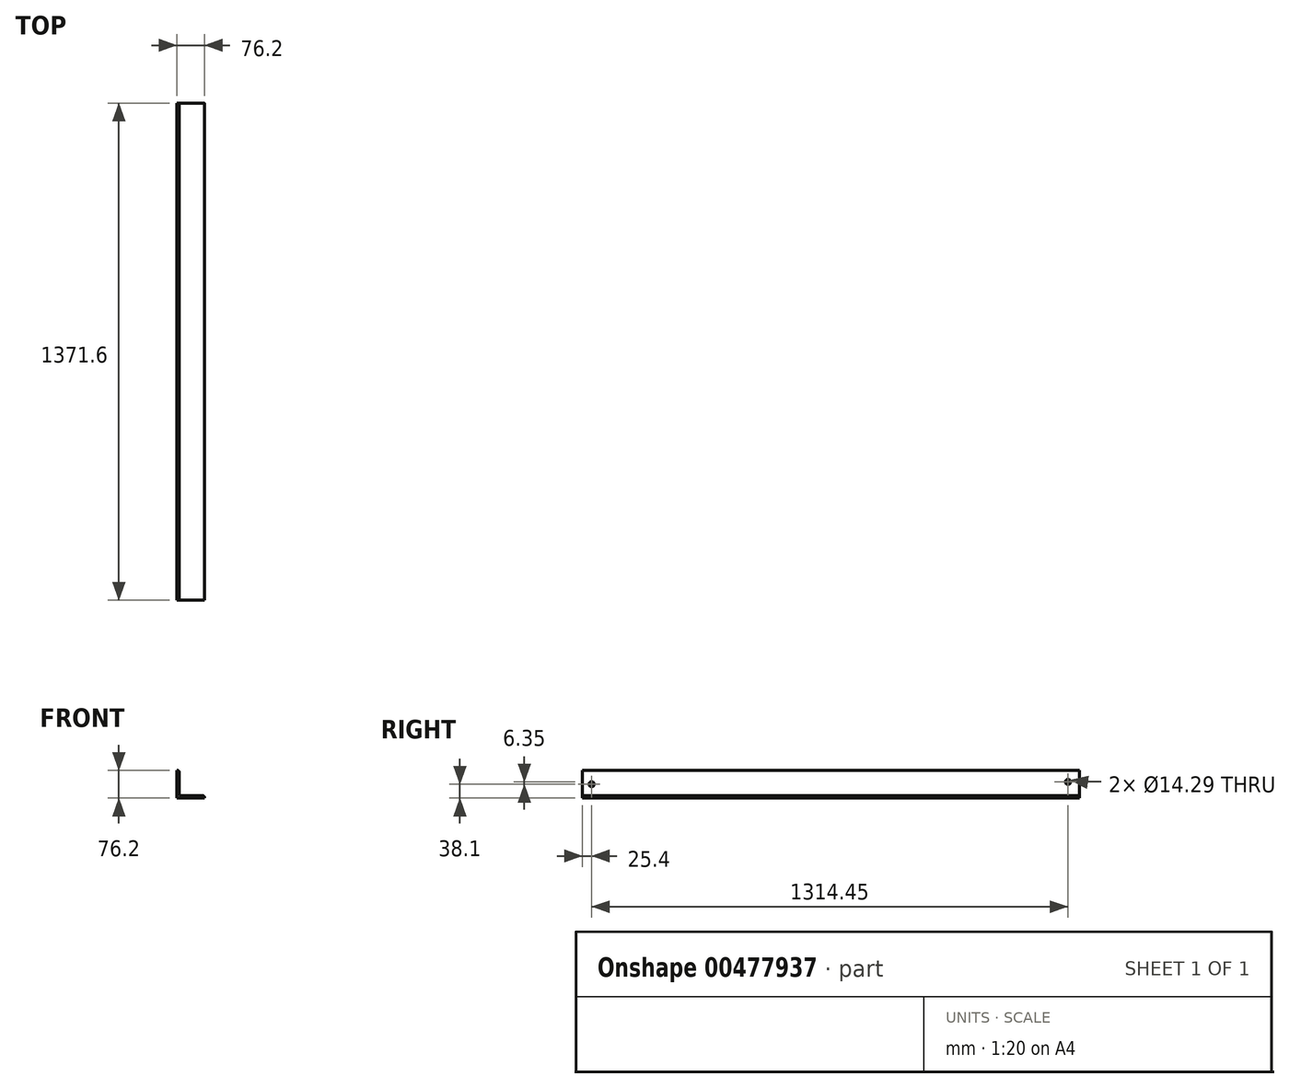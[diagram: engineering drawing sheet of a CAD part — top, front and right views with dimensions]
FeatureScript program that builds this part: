
annotation { "Feature Type Name" : "Feature", "Feature Type Description" : "" }
export const myFeature = defineFeature(function(context is Context, id is Id, definition is map)
    precondition{}
    {
        {
            var Q0;
            Q0=qCreatedBy(makeId("Front.planeOp"),FACE);
            var sketch = newSketch(context, id + "F0", { "sketchPlane" : qUnion([Q0])});
            skLineSegment(sketch, "E0.bottom", {"start": v(-31.75, 38.1) * mm, "end": v(-38.1, 38.1) * mm});
            skLineSegment(sketch, "E0.top", {"start": v(38.1, -38.1) * mm, "end": v(-38.1, -38.1) * mm});
            skLineSegment(sketch, "E0.left", {"start": v(38.1, -31.75) * mm, "end": v(38.1, -38.1) * mm});
            skLineSegment(sketch, "E0.right", {"start": v(-38.1, 38.1) * mm, "end": v(-38.1, -38.1) * mm});
            skPoint(sketch, "E0.middle", {"position": v(0, 0) * mm});
            skLineSegment(sketch, "E1.0", {"start": v(-31.75, 38.1) * mm, "end": v(-31.75, -31.75) * mm});
            skLineSegment(sketch, "E2.0", {"start": v(38.1, -31.75) * mm, "end": v(-31.75, -31.75) * mm});
            skPoint(sketch, "E3.orphan", {"position": v(38.1, 38.1) * mm});
            skSolve(sketch);
        }
        {
            var Q0;
            Q0 = qSketchRegion(id + "F0", true);
            extrude(context, id + "F1", {"entities" : qUnion([Q0]), "endBound" : BoundingType.SYMMETRIC, "depth" : 1371.6 * mm});
        }
        {
            var Q0;
            Q0=makeQuery(id+"F1.opExtrude","SWEPT_EDGE",EDGE,{"disambiguationData":[OSD([sQuery(id+"F0.wireOp",EDGE,"E1.0"),sQuery(id+"F0.wireOp",EDGE,"E2.0")])]});
            var Q1;
            Q1=makeQuery(id+"F1.opExtrude","SWEPT_EDGE",EDGE,{"disambiguationData":[OSD([sQuery(id+"F0.wireOp",EDGE,"E0.bottom"),sQuery(id+"F0.wireOp",EDGE,"E1.0")])]});
            var Q2;
            Q2=makeQuery(id+"F1.opExtrude","SWEPT_EDGE",EDGE,{"disambiguationData":[OSD([sQuery(id+"F0.wireOp",EDGE,"E0.left"),sQuery(id+"F0.wireOp",EDGE,"E2.0")])]});
            fillet(context, id + "F2", {"entities" : qUnion([Q0, Q1, Q2]), "radius" : 5.08 * mm, "tangentPropagation" : true, "allowEdgeOverflow" : false});
        }
        {
            var Q0;
            Q0=makeQuery(id+"F1.opExtrude","SWEPT_FACE",FACE,{"disambiguationData":[OSD([sQuery(id+"F0.wireOp",EDGE,"E0.right")])]});
            var sketch = newSketch(context, id + "F3", { "sketchPlane" : qUnion([Q0])});
            skPoint(sketch, "E4.centerSnap0", {"position": v(-685.8, 0) * mm});
            skCircle(sketch, "E5", {"center": v(660.4, 0) * mm, "radius": 7.14 * mm});
            skCircle(sketch, "E6", {"center": v(-654.05, 6.35) * mm, "radius": 7.14 * mm});
            skSolve(sketch);
        }
        {
            var Q0;
            Q0 = qSketchRegion(id + "F3", true);
            extrude(context, id + "F4", {"entities" : qUnion([Q0]), "operationType" : NewBodyOperationType.REMOVE, "oppositeDirection" : true, "depth" : 25.4 * mm});
        }
    });
